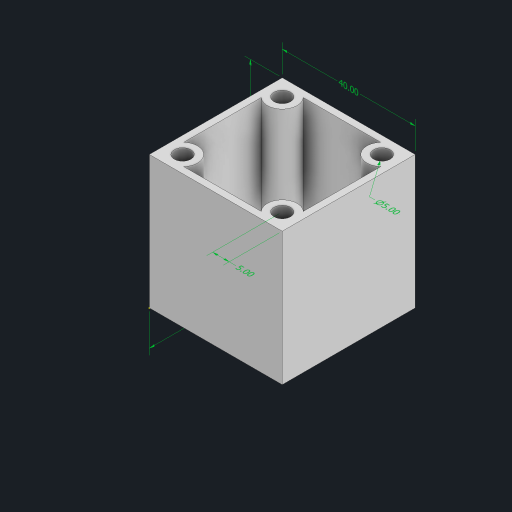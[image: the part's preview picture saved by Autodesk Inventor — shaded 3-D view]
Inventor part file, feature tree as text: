
AUTODESK INVENTOR PART (.ipt)
format: ipt  version: 2023 (Build 270158000, 158)  size: 149,504 bytes
history: native  units: in
note: dims shown in document units (in); Inventor stores cm internally (conversion verified against a paired STEP export)
features: other x7, extrude x2, sketch x2, shell x1
ambient origin geometry x8: Origin, YZ Plane, XZ Plane, XY Plane, X Axis, Y Axis, Z Axis, Center Point
bodies: Solid1 (feature_tree)
feature tree (12):
  other  "Annotations"
  extrude  "Extrusion1"  Depth=1.5748in
  extrude  "Extrusion2"  Depth=1.5748in
  shell  "Shell1"  Thickness=0.1969in
  sketch  "Sketch3"  dims[d6=1.5748in d7=0.0in d8=0.1969in d9=0.1969in d10=0.1969in d11=0.7874in d13=1.1811in d14=0.7874in d16=1.1811in d19=1.9813in d20=0.0in d21=0.0787in d24=0.0in d25=0.3937in d26=1.5748in d27=0.0in d28=0.3937in d29=1.5748in d30=0.0382in d31=0.1969in d34=1.2708in d35=0.1969in d39=0.0in d40=0.3937in d41=1.5748in]
  other  "cube_profile"
  sketch  "Sketch2"  dims[d2=1.5748in d4=1.5748in]
  other  "Linear Dimension 1"
  other  "Linear Dimension 2"
  other  "Linear Dimension 3"
  other  "Diameter Dimension 2"
  other  "Linear Dimension 4"
